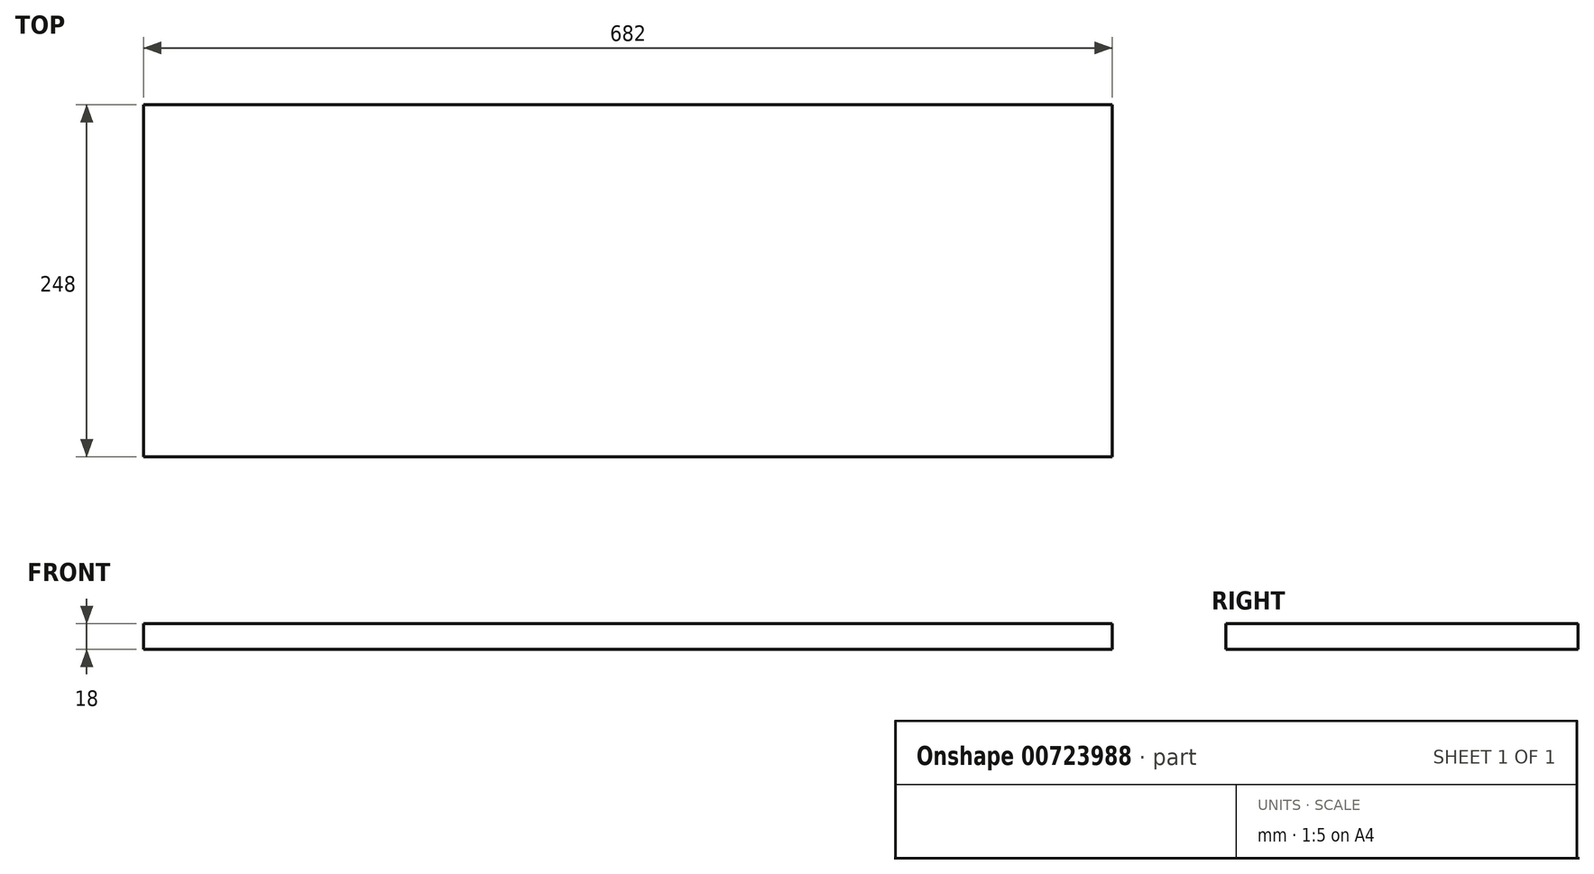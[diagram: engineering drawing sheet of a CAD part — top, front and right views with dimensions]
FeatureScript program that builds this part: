
annotation { "Feature Type Name" : "Feature", "Feature Type Description" : "" }
export const myFeature = defineFeature(function(context is Context, id is Id, definition is map)
    precondition{}
    {
        {
            var Q0;
            Q0=qCreatedBy(makeId("Top.planeOp"),FACE);
            var sketch = newSketch(context, id + "F0", { "sketchPlane" : qUnion([Q0])});
            skLineSegment(sketch, "E0.bottom", {"start": v(-314.08, -149.4) * mm, "end": v(367.92, -149.4) * mm});
            skLineSegment(sketch, "E0.top", {"start": v(-314.08, -397.4) * mm, "end": v(367.92, -397.4) * mm});
            skLineSegment(sketch, "E0.left", {"start": v(-314.08, -149.4) * mm, "end": v(-314.08, -397.4) * mm});
            skLineSegment(sketch, "E0.right", {"start": v(367.92, -149.4) * mm, "end": v(367.92, -397.4) * mm});
            skLineSegment(sketch, "E1", {"start": v(-314.08, -149.4) * mm, "end": v(367.92, -397.4) * mm, "construction": true});
            skLineSegment(sketch, "E2", {"start": v(367.92, -149.4) * mm, "end": v(-314.08, -397.4) * mm, "construction": true});
            skSolve(sketch);
        }
        {
            var Q0;
            Q0=qSketchRegion(id+"F0",true);
            extrude(context, id + "F1", {"entities" : qUnion([Q0]), "depth" : 18 * mm, "offsetDistance" : 25 * mm});
        }
    });
